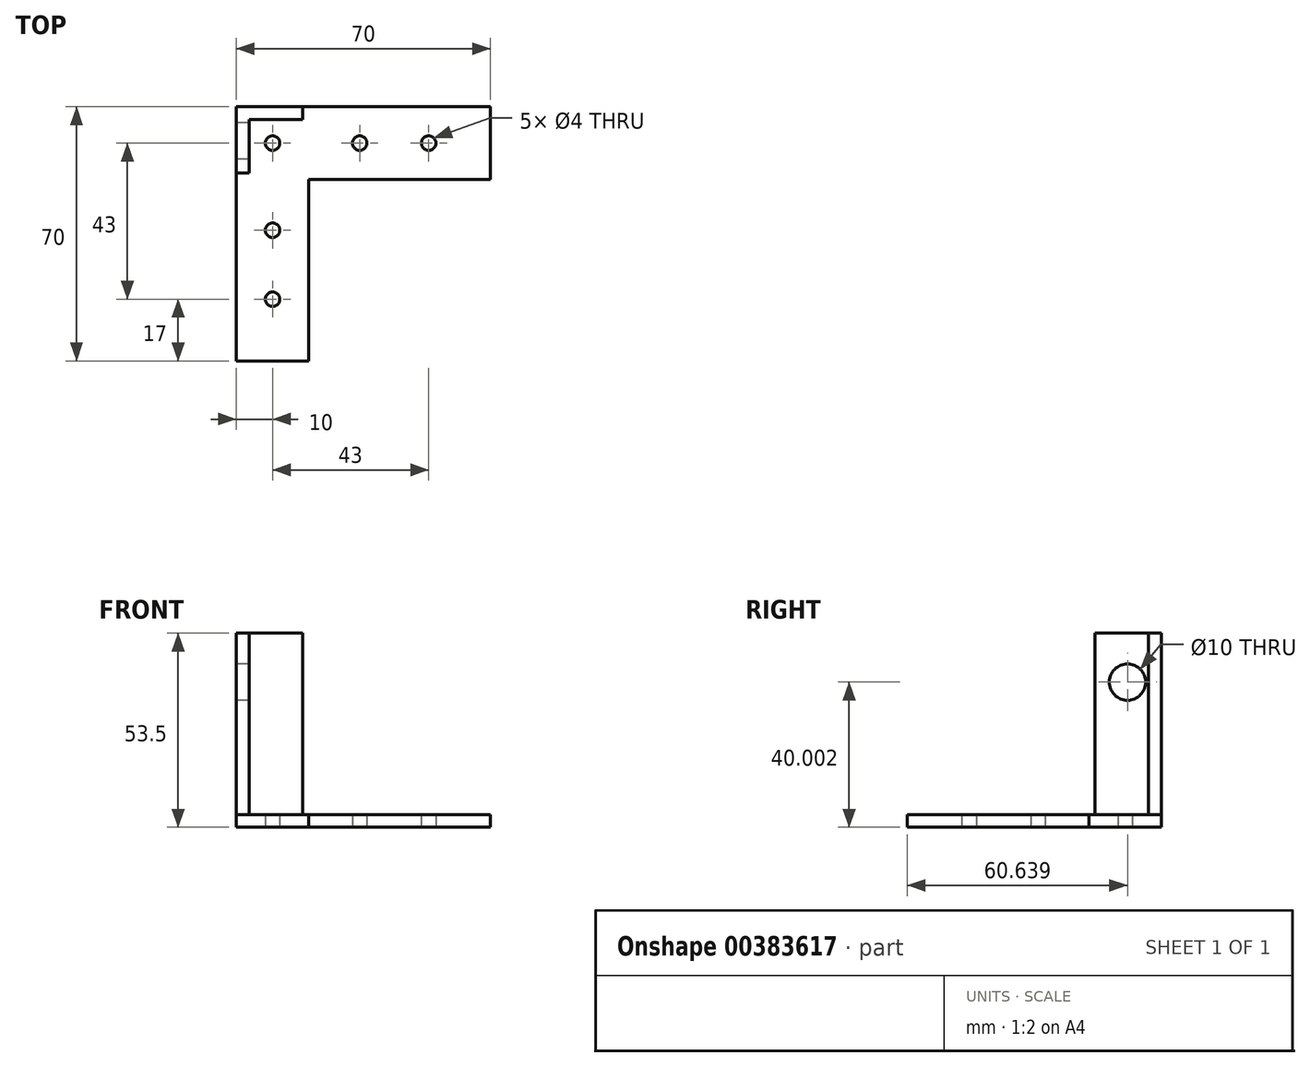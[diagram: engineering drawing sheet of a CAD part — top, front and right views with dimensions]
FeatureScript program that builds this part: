
annotation { "Feature Type Name" : "Feature", "Feature Type Description" : "" }
export const myFeature = defineFeature(function(context is Context, id is Id, definition is map)
    precondition{}
    {
        {
            var Q0;
            Q0=qCreatedBy(makeId("Top.planeOp"),FACE);
            var sketch = newSketch(context, id + "F0", { "sketchPlane" : qUnion([Q0])});
            skLineSegment(sketch, "E0.bottom", {"start": v(-10, -60) * mm, "end": v(10, -60) * mm});
            skLineSegment(sketch, "E0.top", {"start": v(-10, 10) * mm, "end": v(10, 10) * mm});
            skLineSegment(sketch, "E0.left", {"start": v(-10, -60) * mm, "end": v(-10, 10) * mm});
            skLineSegment(sketch, "E0.right", {"start": v(10, -60) * mm, "end": v(10, -10) * mm});
            skLineSegment(sketch, "E1.bottom", {"start": v(-10, 10) * mm, "end": v(60, 10) * mm});
            skLineSegment(sketch, "E1.top", {"start": v(10, -10) * mm, "end": v(60, -10) * mm});
            skLineSegment(sketch, "E1.left", {"start": v(-10, 10) * mm, "end": v(-10, -10) * mm});
            skLineSegment(sketch, "E1.right", {"start": v(60, 10) * mm, "end": v(60, -10) * mm});
            skLineSegment(sketch, "E2", {"start": v(60, 0) * mm, "end": v(-10, 0) * mm, "construction": true});
            skLineSegment(sketch, "E3", {"start": v(0, -60) * mm, "end": v(0, 10) * mm, "construction": true});
            skLineSegment(sketch, "E4", {"start": v(10, -10) * mm, "end": v(-10, -10) * mm, "construction": true});
            skLineSegment(sketch, "E5", {"start": v(10, 10) * mm, "end": v(10, -10) * mm, "construction": true});
            skPoint(sketch, "E6", {"position": v(0, 0) * mm});
            skPoint(sketch, "E7", {"position": v(0, -43) * mm});
            skPoint(sketch, "E8", {"position": v(0, -24) * mm});
            skPoint(sketch, "E9", {"position": v(43, 0) * mm});
            skCircle(sketch, "E10", {"center": v(43, 0) * mm, "radius": 2 * mm});
            skCircle(sketch, "E11", {"center": v(0, -24) * mm, "radius": 2 * mm});
            skCircle(sketch, "E12", {"center": v(0, -43) * mm, "radius": 2 * mm});
            skPoint(sketch, "E13", {"position": v(24, 0) * mm});
            skCircle(sketch, "E14", {"center": v(24, 0) * mm, "radius": 2 * mm});
            skCircle(sketch, "E15", {"center": v(0, 0) * mm, "radius": 2 * mm});
            skSolve(sketch);
        }
        {
            var Q0;
            Q0=makeQuery(id+"F0.imprint","IMPRINT",FACE,{"disambiguationData":[TD([[makeQuery(id+"F0.imprint","IMPRINT",EDGE,{"derivedFrom":sQuery(id+"F0.wireOp",EDGE,"E0.bottom")}),1.0]])]});
            extrude(context, id + "F1", {"entities" : qUnion([Q0]), "depth" : 3.5 * mm});
        }
        {
            var Q0;
            Q0=makeQuery(id+"F1.opExtrude","CAP_FACE",FACE,{"disambiguationData":[OSD([sQuery(id+"F0.wireOp",EDGE,"E0.bottom"),sQuery(id+"F0.wireOp",EDGE,"E0.left"),sQuery(id+"F0.wireOp",EDGE,"E0.right"),sQuery(id+"F0.wireOp",EDGE,"E1.bottom"),sQuery(id+"F0.wireOp",EDGE,"E1.top"),sQuery(id+"F0.wireOp",EDGE,"E1.left"),sQuery(id+"F0.wireOp",EDGE,"E1.right"),sQuery(id+"F0.wireOp",EDGE,"E10"),sQuery(id+"F0.wireOp",EDGE,"E11"),sQuery(id+"F0.wireOp",EDGE,"E12"),sQuery(id+"F0.wireOp",EDGE,"E14"),sQuery(id+"F0.wireOp",EDGE,"E15")])],"isStart":false});
            var sketch = newSketch(context, id + "F2", { "sketchPlane" : qUnion([Q0])});
            skLineSegment(sketch, "E16.0", {"start": v(-10, 10) * mm, "end": v(8.29, 10) * mm});
            skLineSegment(sketch, "E17.0", {"start": v(-10, 10) * mm, "end": v(-10, -8.29) * mm});
            skLineSegment(sketch, "E18", {"start": v(8.29, 10) * mm, "end": v(8.29, 6.46) * mm});
            skLineSegment(sketch, "E19", {"start": v(-6.46, -8.29) * mm, "end": v(-10, -8.29) * mm});
            skPoint(sketch, "E20.orphan", {"position": v(60, 10) * mm});
            skPoint(sketch, "E21.orphan", {"position": v(-10, -60) * mm});
            skLineSegment(sketch, "E22", {"start": v(8.29, 6.46) * mm, "end": v(-6.46, 6.46) * mm});
            skLineSegment(sketch, "E23", {"start": v(-6.46, 6.46) * mm, "end": v(-6.46, -8.29) * mm});
            skSolve(sketch);
        }
        {
            var Q0;
            Q0=makeQuery(id+"F2.imprint","IMPRINT",FACE,{"disambiguationData":[TD([[makeQuery(id+"F2.imprint","IMPRINT",EDGE,{"derivedFrom":sQuery(id+"F2.wireOp",EDGE,"E16.0")}),-1.0]])]});
            extrude(context, id + "F3", {"entities" : qUnion([Q0]), "operationType" : NewBodyOperationType.ADD, "depth" : 50 * mm});
        }
        {
            var Q0;
            Q0=makeQuery(id+"F3.boolean.opBoolean","MERGE",FACE,{"derivedFrom":[makeQuery(id+"F1.opExtrude","SWEPT_FACE",FACE,{"disambiguationData":[OSD([sQuery(id+"F0.wireOp",EDGE,"E0.left"),sQuery(id+"F0.wireOp",EDGE,"E1.left")])]}),makeQuery(id+"F3.opExtrude","SWEPT_FACE",FACE,{"disambiguationData":[OSD([sQuery(id+"F2.wireOp",EDGE,"E17.0")])]})]});
            var sketch = newSketch(context, id + "F4", { "sketchPlane" : qUnion([Q0])});
            skPoint(sketch, "E24.0", {"position": v(-0.86, 53.5) * mm});
            skLineSegment(sketch, "E25", {"start": v(-0.86, 53.5) * mm, "end": v(0, 0) * mm, "construction": true});
            skPoint(sketch, "E26", {"position": v(-0.64, 40) * mm});
            skCircle(sketch, "E27", {"center": v(-0.64, 40) * mm, "radius": 5 * mm});
            skPoint(sketch, "E28.0", {"position": v(0, 0) * mm});
            skSolve(sketch);
        }
        {
            var Q0;
            Q0=makeQuery(id+"F4.imprint","IMPRINT",FACE,{"disambiguationData":[TD([[makeQuery(id+"F4.imprint","IMPRINT",EDGE,{"derivedFrom":sQuery(id+"F4.wireOp",EDGE,"E27")}),1.0]])]});
            extrude(context, id + "F5", {"entities" : qUnion([Q0]), "operationType" : NewBodyOperationType.REMOVE, "endBound" : BoundingType.THROUGH_ALL, "oppositeDirection" : true, "depth" : 25 * mm});
        }
    });
